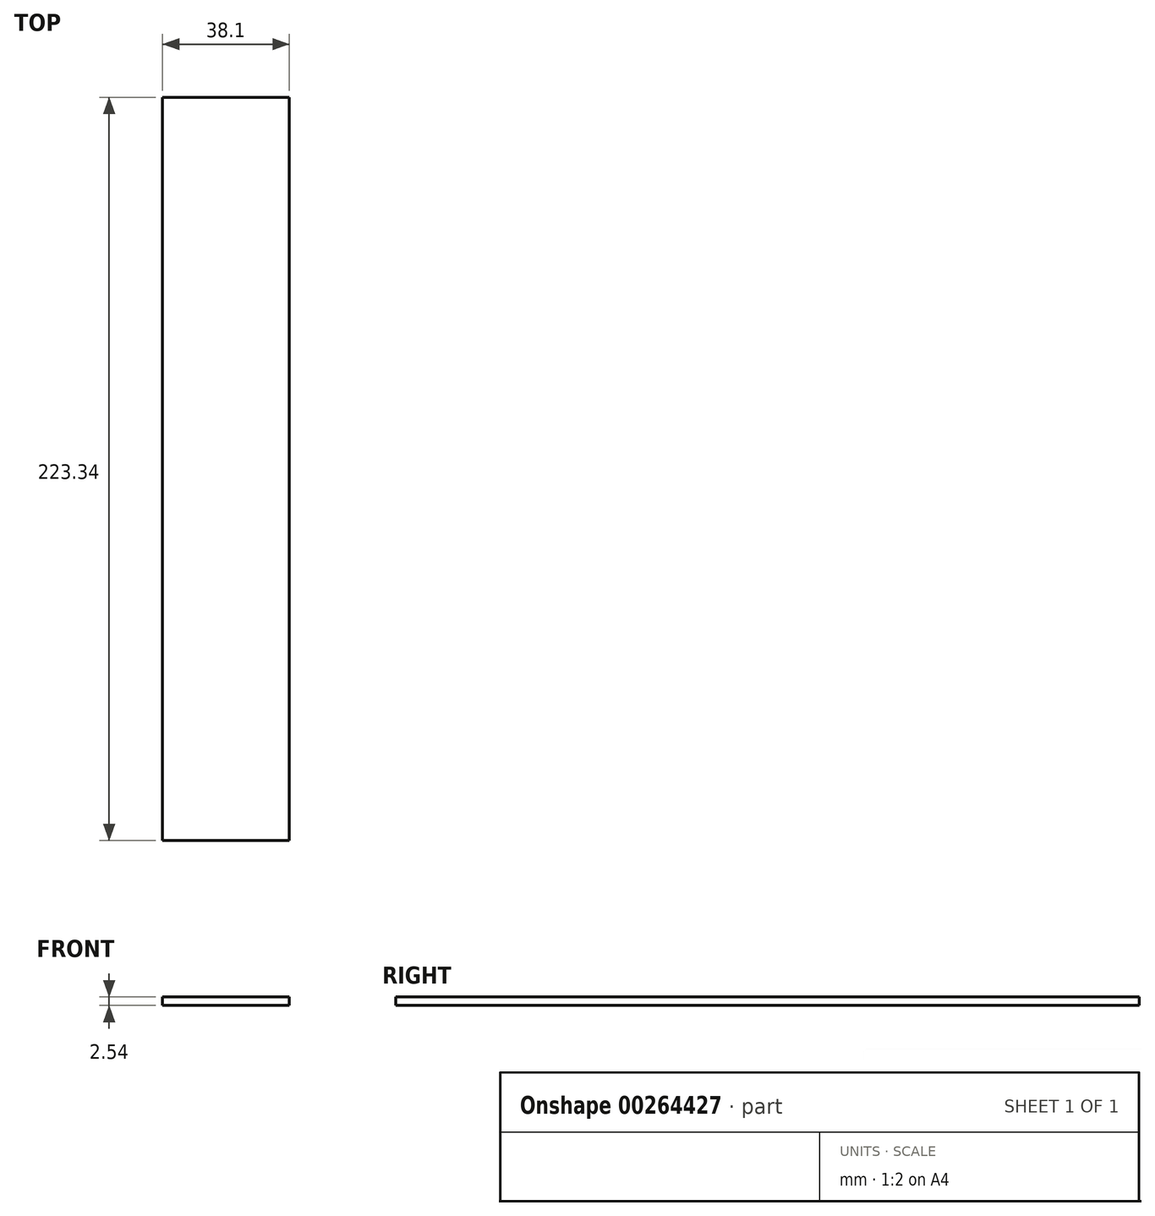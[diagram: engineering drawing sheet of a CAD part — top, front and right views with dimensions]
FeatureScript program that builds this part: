
annotation { "Feature Type Name" : "Feature", "Feature Type Description" : "" }
export const myFeature = defineFeature(function(context is Context, id is Id, definition is map)
    precondition{}
    {
        {
            var Q0;
            Q0=qCreatedBy(makeId("Top.planeOp"),FACE);
            var sketch = newSketch(context, id + "F0", { "sketchPlane" : qUnion([Q0])});
            skLineSegment(sketch, "E0.bottom", {"start": v(-18.42, 189.06) * mm, "end": v(19.68, 189.06) * mm});
            skLineSegment(sketch, "E1", {"start": v(-18.42, -34.28) * mm, "end": v(19.67, -34.28) * mm});
            skLineSegment(sketch, "E2", {"start": v(-18.42, 189.06) * mm, "end": v(-18.42, -34.28) * mm});
            skLineSegment(sketch, "E3", {"start": v(19.68, 189.06) * mm, "end": v(19.67, -34.28) * mm});
            skSolve(sketch);
        }
        {
            var Q0;
            Q0=makeQuery(id+"F0.imprint","IMPRINT",FACE,{"disambiguationData":[TD([[makeQuery(id+"F0.imprint","IMPRINT",EDGE,{"derivedFrom":sQuery(id+"F0.wireOp",EDGE,"E0.bottom")}),-1.0]])]});
            extrude(context, id + "F1", {"entities" : qUnion([Q0]), "depth" : 2.54 * mm});
        }
    });
